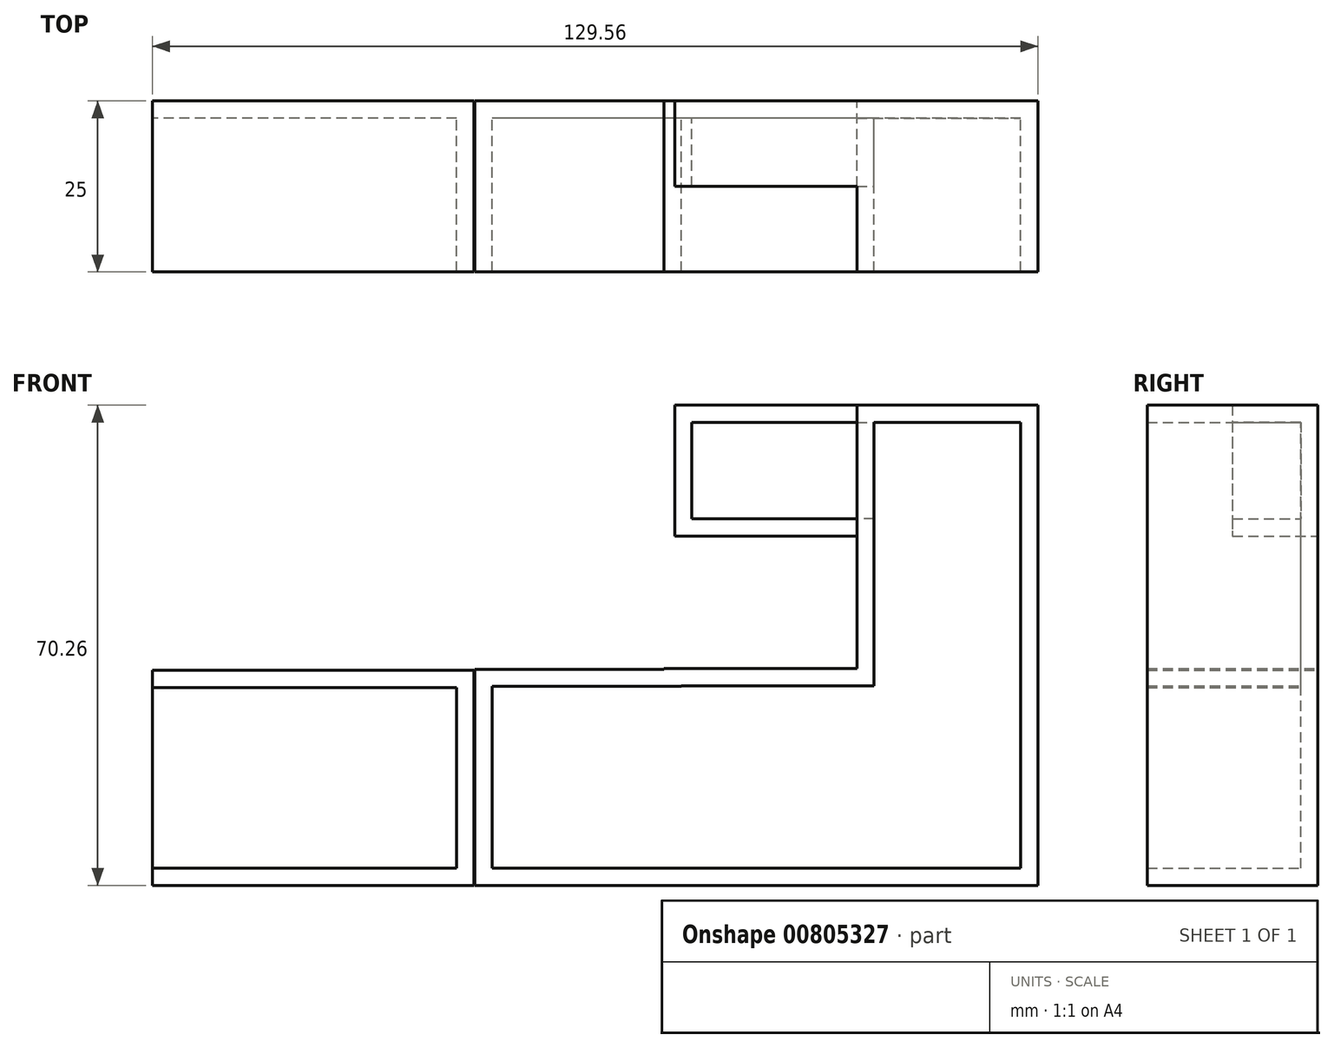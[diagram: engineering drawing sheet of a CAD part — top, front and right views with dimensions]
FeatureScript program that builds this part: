
annotation { "Feature Type Name" : "Feature", "Feature Type Description" : "" }
export const myFeature = defineFeature(function(context is Context, id is Id, definition is map)
    precondition{}
    {
        {
            var Q0;
            Q0=qCreatedBy(makeId("Front.planeOp"),FACE);
            var sketch = newSketch(context, id + "F0", { "sketchPlane" : qUnion([Q0])});
            skLineSegment(sketch, "E0.bottom", {"start": v(0, 0) * mm, "end": v(26.46, 0) * mm});
            skLineSegment(sketch, "E0.top", {"start": v(0, 70.26) * mm, "end": v(26.46, 70.26) * mm});
            skLineSegment(sketch, "E0.left", {"start": v(0, 0) * mm, "end": v(0, 70.26) * mm});
            skLineSegment(sketch, "E0.right", {"start": v(26.46, 0) * mm, "end": v(26.46, 70.26) * mm});
            skLineSegment(sketch, "E1.bottom", {"start": v(0, 0) * mm, "end": v(-28.22, 0) * mm});
            skLineSegment(sketch, "E1.top", {"start": v(0, 31.7) * mm, "end": v(-28.22, 31.7) * mm});
            skLineSegment(sketch, "E1.left", {"start": v(0, 0) * mm, "end": v(0, 31.7) * mm});
            skLineSegment(sketch, "E1.right", {"start": v(-28.22, 0) * mm, "end": v(-28.22, 31.7) * mm});
            skSolve(sketch);
        }
        {
            var Q0;
            Q0=makeQuery(id+"F0.imprint","IMPRINT",FACE,{"disambiguationData":[TD([[makeQuery(id+"F0.imprint","IMPRINT",EDGE,{"derivedFrom":sQuery(id+"F0.wireOp",EDGE,"E1.bottom")}),-1.0]])]});
            var Q1;
            Q1=makeQuery(id+"F0.imprint","IMPRINT",FACE,{"disambiguationData":[TD([[makeQuery(id+"F0.imprint","IMPRINT",EDGE,{"derivedFrom":sQuery(id+"F0.wireOp",EDGE,"E0.bottom")}),1.0]])]});
            extrude(context, id + "F1", {"entities" : qUnion([Q0, Q1]), "depth" : 25 * mm, "offsetDistance" : 25 * mm});
        }
        {
            var Q0;
            Q0=qCreatedBy(makeId("Front.planeOp"),FACE);
            var sketch = newSketch(context, id + "F2", { "sketchPlane" : qUnion([Q0])});
            skLineSegment(sketch, "E2.0.0", {"start": v(-28.22, 0) * mm, "end": v(26.46, 0) * mm});
            skLineSegment(sketch, "E2.0.1", {"start": v(26.46, 0) * mm, "end": v(26.46, 70.26) * mm});
            skLineSegment(sketch, "E2.0.2", {"start": v(26.46, 70.26) * mm, "end": v(0, 70.26) * mm});
            skLineSegment(sketch, "E2.0.3", {"start": v(0, 70.26) * mm, "end": v(0, 31.7) * mm});
            skLineSegment(sketch, "E2.0.4", {"start": v(0, 31.7) * mm, "end": v(-28.22, 31.7) * mm});
            skLineSegment(sketch, "E2.0.5", {"start": v(-28.22, 31.7) * mm, "end": v(-28.22, 0) * mm});
            skLineSegment(sketch, "E3.bottom", {"start": v(-28.22, 0) * mm, "end": v(-55.92, 0) * mm});
            skLineSegment(sketch, "E3.top", {"start": v(-28.22, 31.62) * mm, "end": v(-55.92, 31.62) * mm});
            skLineSegment(sketch, "E3.left", {"start": v(-28.22, 0) * mm, "end": v(-28.22, 31.62) * mm});
            skLineSegment(sketch, "E3.right", {"start": v(-55.92, 0) * mm, "end": v(-55.92, 31.62) * mm});
            skSolve(sketch);
        }
        {
            var Q0;
            Q0 = qSketchRegion(id + "F2", true);
            extrude(context, id + "F3", {"entities" : qUnion([Q0]), "operationType" : NewBodyOperationType.ADD, "depth" : 25 * mm, "offsetDistance" : 25 * mm});
        }
        {
            var Q0;
            Q0=qCreatedBy(makeId("Front.planeOp"),FACE);
            var sketch = newSketch(context, id + "F4", { "sketchPlane" : qUnion([Q0])});
            skLineSegment(sketch, "E4.bottom", {"start": v(-56.09, 0) * mm, "end": v(-78.1, 0) * mm});
            skLineSegment(sketch, "E4.top", {"start": v(-56.09, 31.46) * mm, "end": v(-78.1, 31.46) * mm});
            skLineSegment(sketch, "E4.left", {"start": v(-56.09, 0) * mm, "end": v(-56.09, 31.46) * mm});
            skLineSegment(sketch, "E4.right", {"start": v(-78.1, 0) * mm, "end": v(-78.1, 31.46) * mm});
            skSolve(sketch);
        }
        {
            var Q0;
            Q0 = qSketchRegion(id + "F4", true);
            extrude(context, id + "F5", {"entities" : qUnion([Q0]), "depth" : 25 * mm, "offsetDistance" : 25 * mm});
        }
        {
            var Q0;
            Q0=makeQuery(id+"F5.opExtrude","SWEPT_FACE",FACE,{"disambiguationData":[OSD([sQuery(id+"F4.wireOp",EDGE,"E4.right")])]});
            extrude(context, id + "F6", {"entities" : qUnion([Q0]), "operationType" : NewBodyOperationType.ADD, "depth" : 25 * mm, "offsetDistance" : 25 * mm});
        }
        {
            var Q0;
            Q0=qCreatedBy(makeId("Front.planeOp"),FACE);
            var sketch = newSketch(context, id + "F7", { "sketchPlane" : qUnion([Q0])});
            skLineSegment(sketch, "E5.bottom", {"start": v(0, 70.25) * mm, "end": v(-26.67, 70.25) * mm});
            skLineSegment(sketch, "E5.top", {"start": v(0, 51.1) * mm, "end": v(-26.67, 51.1) * mm});
            skLineSegment(sketch, "E5.left", {"start": v(0, 70.25) * mm, "end": v(0, 51.1) * mm});
            skLineSegment(sketch, "E5.right", {"start": v(-26.67, 70.25) * mm, "end": v(-26.67, 51.1) * mm});
            skSolve(sketch);
        }
        {
            var Q0;
            Q0 = qSketchRegion(id + "F7", true);
            extrude(context, id + "F8", {"entities" : qUnion([Q0]), "operationType" : NewBodyOperationType.ADD, "depth" : 12.5 * mm, "offsetDistance" : 25 * mm});
        }
        {
            var Q0;
            Q0=makeQuery(id+"F6.opExtrude","CAP_FACE",FACE,{"disambiguationData":[OSD([sQuery(id+"F4.wireOp",EDGE,"E4.right")])],"isStart":false});
            var Q1;
            Q1=makeQuery(id+"F8.opExtrude","CAP_FACE",FACE,{"disambiguationData":[OSD([sQuery(id+"F7.wireOp",EDGE,"E5.bottom"),sQuery(id+"F7.wireOp",EDGE,"E5.top"),sQuery(id+"F7.wireOp",EDGE,"E5.left"),sQuery(id+"F7.wireOp",EDGE,"E5.right")])],"isStart":false});
            var Q2;
            Q2=makeQuery(id+"F3.boolean.opBoolean","MERGE",FACE,{"derivedFrom":[makeQuery(id+"F1.opExtrude","CAP_FACE",FACE,{"disambiguationData":[OSD([sQuery(id+"F0.wireOp",EDGE,"E0.bottom"),sQuery(id+"F0.wireOp",EDGE,"E0.top"),sQuery(id+"F0.wireOp",EDGE,"E0.left"),sQuery(id+"F0.wireOp",EDGE,"E0.right"),sQuery(id+"F0.wireOp",EDGE,"E1.bottom"),sQuery(id+"F0.wireOp",EDGE,"E1.top"),sQuery(id+"F0.wireOp",EDGE,"E1.right")])],"isStart":false}),makeQuery(id+"F3.opExtrude","CAP_FACE",FACE,{"disambiguationData":[OSD([sQuery(id+"F2.wireOp",EDGE,"E2.0.0"),sQuery(id+"F2.wireOp",EDGE,"E2.0.1"),sQuery(id+"F2.wireOp",EDGE,"E2.0.2"),sQuery(id+"F2.wireOp",EDGE,"E2.0.3"),sQuery(id+"F2.wireOp",EDGE,"E2.0.4"),sQuery(id+"F2.wireOp",EDGE,"E2.0.5"),sQuery(id+"F2.wireOp",EDGE,"E3.bottom"),sQuery(id+"F2.wireOp",EDGE,"E3.top"),sQuery(id+"F2.wireOp",EDGE,"E3.right")])],"isStart":false})]});
            var Q3;
            {var subQ0=sQuery(id+"F4.wireOp",EDGE,"E4.right");Q3=makeQuery(id+"F6.boolean.opBoolean","MERGE",FACE,{"derivedFrom":[makeQuery(id+"F5.opExtrude","CAP_FACE",FACE,{"disambiguationData":[OSD([sQuery(id+"F4.wireOp",EDGE,"E4.bottom"),sQuery(id+"F4.wireOp",EDGE,"E4.top"),sQuery(id+"F4.wireOp",EDGE,"E4.left"),subQ0])],"isStart":false}),makeQuery(id+"F6.opExtrude","SWEPT_FACE",FACE,{"disambiguationData":[OSD([subQ0]),TDD([makeQuery(id+"F5.opExtrude","CAP_EDGE",EDGE,{"disambiguationData":[OSD([subQ0])],"isStart":false})])]})]});}
            shell(context, id + "F9", {"entities" : qUnion([Q0, Q1, Q2, Q3]), "thickness" : 2.5 * mm});
        }
    });
